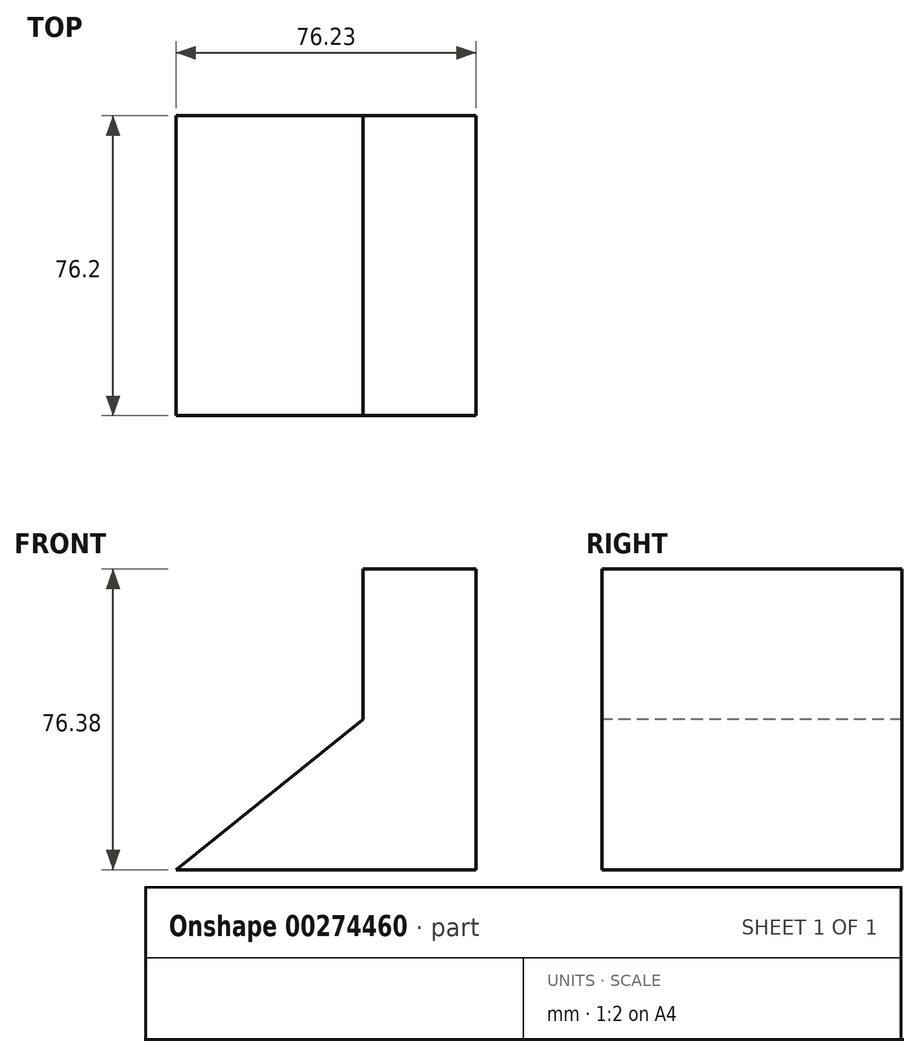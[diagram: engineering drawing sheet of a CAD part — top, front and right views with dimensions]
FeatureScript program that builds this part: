
annotation { "Feature Type Name" : "Feature", "Feature Type Description" : "" }
export const myFeature = defineFeature(function(context is Context, id is Id, definition is map)
    precondition{}
    {
        {
            var Q0;
            Q0=qCreatedBy(makeId("Front.planeOp"),FACE);
            var sketch = newSketch(context, id + "F0", { "sketchPlane" : qUnion([Q0])});
            skLineSegment(sketch, "E0.bottom", {"start": v(0, 0) * mm, "end": v(-76.23, 0) * mm});
            skLineSegment(sketch, "E0.top", {"start": v(0, 76.38) * mm, "end": v(-76.23, 76.38) * mm});
            skLineSegment(sketch, "E0.left", {"start": v(0, 0) * mm, "end": v(0, 76.38) * mm});
            skLineSegment(sketch, "E0.right", {"start": v(-76.23, 0) * mm, "end": v(-76.23, 76.38) * mm});
            skSolve(sketch);
        }
        {
            var Q0;
            Q0 = qSketchRegion(id + "F0", true);
            extrude(context, id + "F1", {"entities" : qUnion([Q0]), "depth" : 76.2 * mm});
        }
        {
            var Q0;
            Q0=makeQuery(id+"F1.opExtrude","CAP_FACE",FACE,{"disambiguationData":[OSD([sQuery(id+"F0.wireOp",EDGE,"E0.bottom"),sQuery(id+"F0.wireOp",EDGE,"E0.top"),sQuery(id+"F0.wireOp",EDGE,"E0.left"),sQuery(id+"F0.wireOp",EDGE,"E0.right")])],"isStart":false});
            var sketch = newSketch(context, id + "F2", { "sketchPlane" : qUnion([Q0])});
            skLineSegment(sketch, "E1.bottom", {"start": v(-28.74, 76.38) * mm, "end": v(-76.23, 76.38) * mm});
            skLineSegment(sketch, "E1.top", {"start": v(-28.74, 38.2) * mm, "end": v(-76.23, 38.2) * mm});
            skLineSegment(sketch, "E1.left", {"start": v(-28.74, 76.38) * mm, "end": v(-28.74, 38.2) * mm});
            skLineSegment(sketch, "E1.right", {"start": v(-76.23, 76.38) * mm, "end": v(-76.23, 38.2) * mm});
            skSolve(sketch);
        }
        {
            var Q0;
            Q0 = qSketchRegion(id + "F2", true);
            extrude(context, id + "F3", {"entities" : qUnion([Q0]), "operationType" : NewBodyOperationType.REMOVE, "oppositeDirection" : true, "depth" : 76.2 * mm});
        }
        {
            var Q0;
            Q0=makeQuery(id+"F1.opExtrude","CAP_FACE",FACE,{"disambiguationData":[OSD([sQuery(id+"F0.wireOp",EDGE,"E0.bottom"),sQuery(id+"F0.wireOp",EDGE,"E0.top"),sQuery(id+"F0.wireOp",EDGE,"E0.left"),sQuery(id+"F0.wireOp",EDGE,"E0.right")])],"isStart":false});
            var sketch = newSketch(context, id + "F4", { "sketchPlane" : qUnion([Q0])});
            skLineSegment(sketch, "E2", {"start": v(-28.74, 38.2) * mm, "end": v(-76.23, 0) * mm});
            skLineSegment(sketch, "E3", {"start": v(-76.23, 0) * mm, "end": v(-76.23, 38.2) * mm});
            skLineSegment(sketch, "E4", {"start": v(-76.23, 38.2) * mm, "end": v(-28.74, 38.2) * mm});
            skSolve(sketch);
        }
        {
            var Q0;
            Q0 = qSketchRegion(id + "F4", true);
            extrude(context, id + "F5", {"entities" : qUnion([Q0]), "operationType" : NewBodyOperationType.REMOVE, "oppositeDirection" : true, "depth" : 76.2 * mm});
        }
    });
